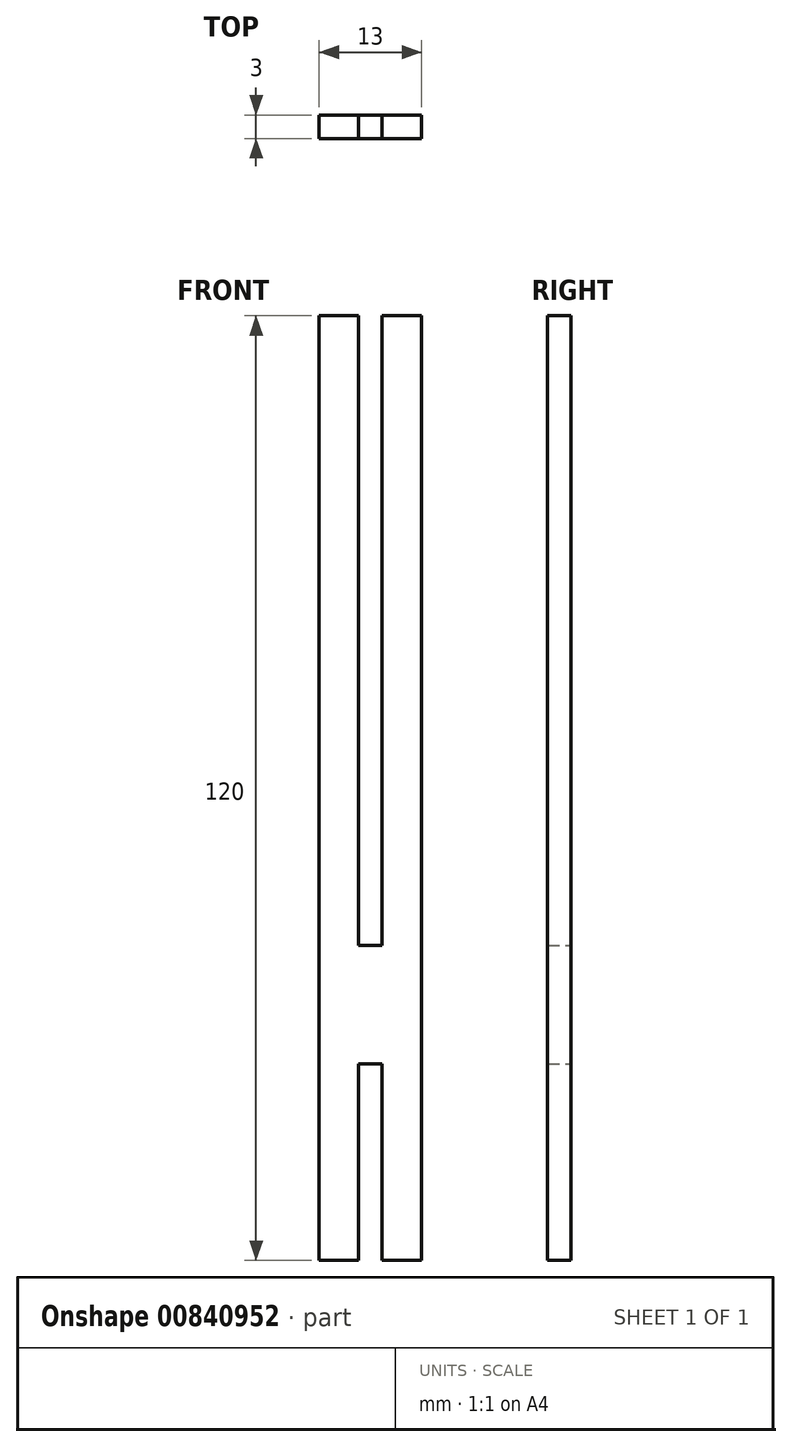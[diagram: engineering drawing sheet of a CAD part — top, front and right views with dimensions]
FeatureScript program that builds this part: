
annotation { "Feature Type Name" : "Feature", "Feature Type Description" : "" }
export const myFeature = defineFeature(function(context is Context, id is Id, definition is map)
    precondition{}
    {
        {
            var Q0;
            Q0=qCreatedBy(makeId("Front.planeOp"),FACE);
            var sketch = newSketch(context, id + "F0", { "sketchPlane" : qUnion([Q0])});
            skLineSegment(sketch, "E0", {"start": v(0, 0) * mm, "end": v(0, 120) * mm});
            skLineSegment(sketch, "E1", {"start": v(0, 120) * mm, "end": v(5, 120) * mm});
            skLineSegment(sketch, "E2", {"start": v(5, 120) * mm, "end": v(5, 40) * mm});
            skLineSegment(sketch, "E3", {"start": v(5, 40) * mm, "end": v(8, 40) * mm});
            skLineSegment(sketch, "E4", {"start": v(8, 40) * mm, "end": v(8, 120) * mm});
            skLineSegment(sketch, "E5", {"start": v(8, 120) * mm, "end": v(13, 120) * mm});
            skLineSegment(sketch, "E6", {"start": v(13, 120) * mm, "end": v(13, 0) * mm});
            skLineSegment(sketch, "E7", {"start": v(13, 0) * mm, "end": v(8, 0) * mm});
            skLineSegment(sketch, "E8", {"start": v(8, 0) * mm, "end": v(8, 25) * mm});
            skLineSegment(sketch, "E9", {"start": v(8, 25) * mm, "end": v(5, 25) * mm});
            skLineSegment(sketch, "E10", {"start": v(5, 25) * mm, "end": v(5, 0) * mm});
            skLineSegment(sketch, "E11", {"start": v(5, 0) * mm, "end": v(0, 0) * mm});
            skSolve(sketch);
        }
        {
            var Q0;
            Q0 = qSketchRegion(id + "F0", true);
            extrude(context, id + "F1", {"entities" : qUnion([Q0]), "depth" : 3 * mm, "offsetDistance" : 25 * mm});
        }
    });
